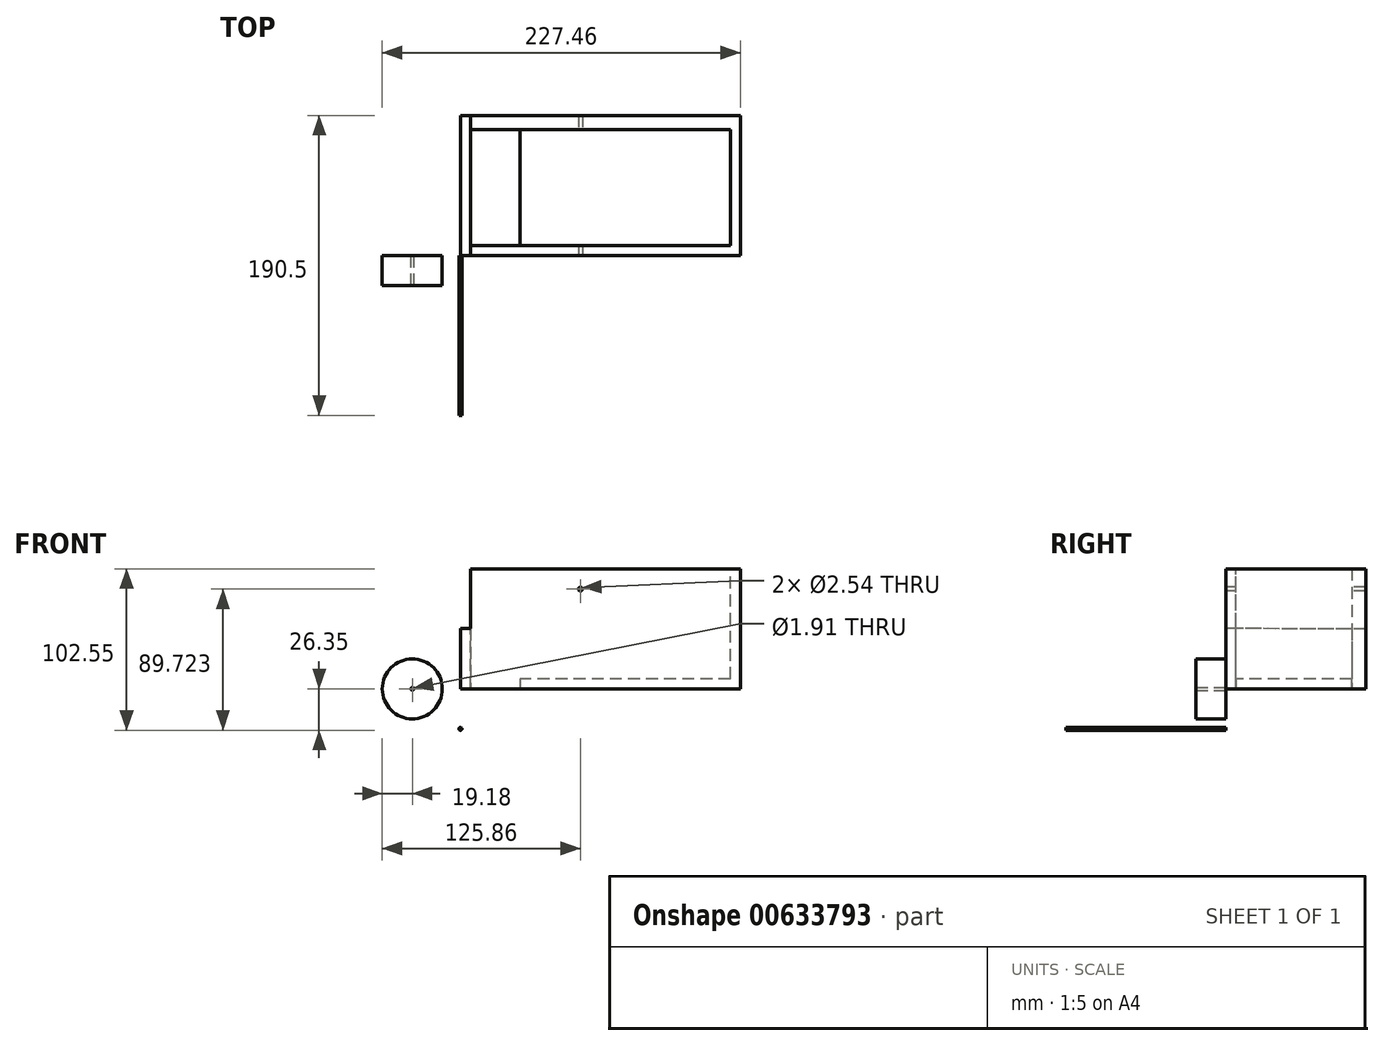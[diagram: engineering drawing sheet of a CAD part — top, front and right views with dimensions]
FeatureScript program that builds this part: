
annotation { "Feature Type Name" : "Feature", "Feature Type Description" : "" }
export const myFeature = defineFeature(function(context is Context, id is Id, definition is map)
    precondition{}
    {
        {
            var Q0;
            Q0=qCreatedBy(makeId("Front.planeOp"),FACE);
            var sketch = newSketch(context, id + "F0", { "sketchPlane" : qUnion([Q0])});
            skLineSegment(sketch, "E0", {"start": v(0, 0) * mm, "end": v(177.8, 0) * mm});
            skLineSegment(sketch, "E1", {"start": v(177.8, 0) * mm, "end": v(177.8, 76.2) * mm});
            skLineSegment(sketch, "E2", {"start": v(177.8, 76.2) * mm, "end": v(0, 76.2) * mm});
            skLineSegment(sketch, "E3", {"start": v(0, 76.2) * mm, "end": v(0, 0) * mm});
            skSolve(sketch);
        }
        {
            var Q0;
            Q0 = qSketchRegion(id + "F0", true);
            extrude(context, id + "F1", {"entities" : qUnion([Q0]), "oppositeDirection" : true, "depth" : 6.35 * mm, "offsetDistance" : 25.4 * mm});
        }
        {
            var Q0;
            Q0=qCreatedBy(makeId("Top.planeOp"),FACE);
            var sketch = newSketch(context, id + "F2", { "sketchPlane" : qUnion([Q0])});
            skLineSegment(sketch, "E4", {"start": v(0, 0) * mm, "end": v(0, 88.9) * mm});
            skLineSegment(sketch, "E5", {"start": v(0, 88.9) * mm, "end": v(177.8, 88.9) * mm});
            skLineSegment(sketch, "E6", {"start": v(177.8, 88.9) * mm, "end": v(177.8, 0) * mm});
            skLineSegment(sketch, "E7", {"start": v(0, 88.9) * mm, "end": v(6.35, 88.9) * mm});
            skLineSegment(sketch, "E8", {"start": v(6.35, 88.9) * mm, "end": v(6.35, 0) * mm});
            skLineSegment(sketch, "E9", {"start": v(0, 88.9) * mm, "end": v(0, 80.01) * mm});
            skLineSegment(sketch, "E10", {"start": v(0, 80.01) * mm, "end": v(171.45, 80.01) * mm});
            skLineSegment(sketch, "E11", {"start": v(171.45, 80.01) * mm, "end": v(171.45, 0) * mm});
            skLineSegment(sketch, "E12", {"start": v(0, 0) * mm, "end": v(6.35, 0) * mm});
            skLineSegment(sketch, "E13", {"start": v(171.45, 80.01) * mm, "end": v(177.8, 80.01) * mm});
            skLineSegment(sketch, "E14", {"start": v(177.8, 80.01) * mm, "end": v(171.45, 80.01) * mm});
            skLineSegment(sketch, "E15", {"start": v(171.45, 88.9) * mm, "end": v(171.45, 0) * mm});
            skLineSegment(sketch, "E16", {"start": v(177.8, 0) * mm, "end": v(171.45, 0) * mm});
            skSolve(sketch);
        }
        {
            var Q0;
            Q0 = qSketchRegion(id + "F2", true);
            extrude(context, id + "F3", {"entities" : qUnion([Q0]), "operationType" : NewBodyOperationType.ADD, "depth" : 76.2 * mm, "offsetDistance" : 25.4 * mm});
        }
        {
            var Q0;
            Q0=qCreatedBy(makeId("Top.planeOp"),FACE);
            var sketch = newSketch(context, id + "F4", { "sketchPlane" : qUnion([Q0])});
            skLineSegment(sketch, "E17", {"start": v(177.43, 0) * mm, "end": v(37.73, 0) * mm});
            skLineSegment(sketch, "E18", {"start": v(37.73, 0) * mm, "end": v(37.73, 88.76) * mm});
            skLineSegment(sketch, "E19", {"start": v(37.73, 88.76) * mm, "end": v(177.51, 88.76) * mm});
            skLineSegment(sketch, "E20", {"start": v(177.51, 88.76) * mm, "end": v(177.43, 0) * mm});
            skSolve(sketch);
        }
        {
            var Q0;
            Q0 = qSketchRegion(id + "F4", true);
            extrude(context, id + "F5", {"entities" : qUnion([Q0]), "operationType" : NewBodyOperationType.ADD, "depth" : 6.35 * mm, "offsetDistance" : 25.4 * mm});
        }
        {
            var Q0;
            Q0=qCreatedBy(makeId("Right.planeOp"),FACE);
            var sketch = newSketch(context, id + "F6", { "sketchPlane" : qUnion([Q0])});
            skLineSegment(sketch, "E21", {"start": v(0, 0) * mm, "end": v(0, 38.1) * mm});
            skLineSegment(sketch, "E22", {"start": v(0, 38.1) * mm, "end": v(0, 76.2) * mm});
            skLineSegment(sketch, "E23", {"start": v(0, 76.2) * mm, "end": v(88.9, 76.2) * mm});
            skLineSegment(sketch, "E24", {"start": v(88.9, 76.2) * mm, "end": v(88.9, 38.1) * mm});
            skLineSegment(sketch, "E25", {"start": v(88.9, 38.1) * mm, "end": v(0, 38.1) * mm});
            skSolve(sketch);
        }
        {
            var Q0;
            Q0=makeQuery(id+"F6.imprint","IMPRINT",FACE,{"disambiguationData":[TD([[makeQuery(id+"F6.imprint","IMPRINT",EDGE,{"derivedFrom":sQuery(id+"F6.wireOp",EDGE,"E22")}),-1.0]])]});
            extrude(context, id + "F7", {"entities" : qUnion([Q0]), "operationType" : NewBodyOperationType.REMOVE, "oppositeDirection" : true, "depth" : 6.35 * mm, "offsetDistance" : 25.4 * mm});
        }
        {
            var Q0;
            Q0=qCreatedBy(makeId("Front.planeOp"),FACE);
            var sketch = newSketch(context, id + "F8", { "sketchPlane" : qUnion([Q0])});
            skLineSegment(sketch, "E26", {"start": v(0, 76.07) * mm, "end": v(76.2, 76.07) * mm});
            skLineSegment(sketch, "E27", {"start": v(76.2, 76.07) * mm, "end": v(76.2, 63.37) * mm});
            skCircle(sketch, "E28", {"center": v(76.2, 63.37) * mm, "radius": 1.27 * mm});
            skSolve(sketch);
        }
        {
            var Q0;
            Q0=qCreatedBy(makeId("Front.planeOp"),FACE);
            var sketch = newSketch(context, id + "F9", { "sketchPlane" : qUnion([Q0])});
            skLineSegment(sketch, "E29", {"start": v(-5.2, 0) * mm, "end": v(-30.6, 0) * mm});
            skCircle(sketch, "E30", {"center": v(-30.6, 0) * mm, "radius": 19.05 * mm});
            skLineSegment(sketch, "E31", {"start": v(0, 76.7) * mm, "end": v(76.2, 76.7) * mm});
            skLineSegment(sketch, "E32", {"start": v(76.2, 76.7) * mm, "end": v(76.2, 70.35) * mm});
            skCircle(sketch, "E33", {"center": v(76.2, 70.35) * mm, "radius": 1.27 * mm});
            skSolve(sketch);
        }
        {
            var Q0;
            Q0=makeQuery(id+"F9.imprint","IMPRINT",FACE,{"disambiguationData":[TD([[makeQuery(id+"F9.imprint","IMPRINT",EDGE,{"derivedFrom":sQuery(id+"F9.wireOp",EDGE,"E30")}),1.0]])]});
            extrude(context, id + "F10", {"entities" : qUnion([Q0]), "depth" : 19.05 * mm, "offsetDistance" : 25.4 * mm});
        }
        {
            var Q0;
            Q0=makeQuery(id+"F8.imprint","IMPRINT",FACE,{"disambiguationData":[TD([[makeQuery(id+"F8.imprint","IMPRINT",EDGE,{"derivedFrom":sQuery(id+"F8.wireOp",EDGE,"E28")}),1.0]])]});
            extrude(context, id + "F11", {"entities" : qUnion([Q0]), "operationType" : NewBodyOperationType.REMOVE, "oppositeDirection" : true, "depth" : 254 * mm, "offsetDistance" : 25.4 * mm});
        }
        {
            var Q0;
            Q0=qCreatedBy(makeId("Right.planeOp"),FACE);
            var sketch = newSketch(context, id + "F12", { "sketchPlane" : qUnion([Q0])});
            skLineSegment(sketch, "E34", {"start": v(88.84, 0) * mm, "end": v(0, 0) * mm});
            skLineSegment(sketch, "E35", {"start": v(0, 0) * mm, "end": v(0, 76.2) * mm});
            skLineSegment(sketch, "E36", {"start": v(0, 76.2) * mm, "end": v(88.96, 76.2) * mm});
            skLineSegment(sketch, "E37", {"start": v(88.96, 76.2) * mm, "end": v(88.84, 0) * mm});
            skLineSegment(sketch, "E38", {"start": v(88.9, 38.1) * mm, "end": v(0, 38.25) * mm});
            skLineSegment(sketch, "E39", {"start": v(0, 38.25) * mm, "end": v(0, 76.2) * mm});
            skSolve(sketch);
        }
        {
            var Q0;
            {var subQ0=sQuery(id+"F12.wireOp",EDGE,"E36");Q0=makeQuery(id+"F12.imprint","IMPRINT",FACE,{"disambiguationData":[TD([[makeQuery(id+"F12.imprint","IMPRINT",EDGE,{"derivedFrom":subQ0}),-1.0]])]});}
            var sketch = newSketch(context, id + "F13", { "sketchPlane" : qUnion([Q0])});
            skSolve(sketch);
        }
        {
            var Q0;
            {var subQ0=sQuery(id+"F12.wireOp",EDGE,"E36");Q0=makeQuery(id+"F12.imprint","IMPRINT",FACE,{"disambiguationData":[TD([[makeQuery(id+"F12.imprint","IMPRINT",EDGE,{"derivedFrom":subQ0}),-1.0]])]});}
            extrude(context, id + "F14", {"entities" : qUnion([Q0]), "operationType" : NewBodyOperationType.REMOVE, "oppositeDirection" : true, "depth" : 6.35 * mm, "offsetDistance" : 25.4 * mm});
        }
        {
            var Q0;
            {var subQ0=sQuery(id+"F12.wireOp",EDGE,"E36");Q0=makeQuery(id+"F13.imprint","IMPRINT",FACE,{"disambiguationData":[TD([[makeQuery(id+"F13.imprint","IMPRINT",EDGE,{"derivedFrom":makeQuery(id+"F12.imprint","IMPRINT",EDGE,{"derivedFrom":subQ0})}),-1.0]])]});}
            extrude(context, id + "F15", {"entities" : qUnion([Q0]), "operationType" : NewBodyOperationType.REMOVE, "depth" : 6.35 * mm, "offsetDistance" : 25.4 * mm});
        }
        {
            var Q0;
            Q0=qCreatedBy(makeId("Front.planeOp"),FACE);
            var sketch = newSketch(context, id + "F16", { "sketchPlane" : qUnion([Q0])});
            skCircle(sketch, "E40", {"center": v(-30.68, 0) * mm, "radius": 1.27 * mm});
            skSolve(sketch);
        }
        {
            var Q0;
            Q0 = qSketchRegion(id + "F16", true);
            extrude(context, id + "F17", {"entities" : qUnion([Q0]), "operationType" : NewBodyOperationType.REMOVE, "oppositeDirection" : true, "depth" : 76.2 * mm, "offsetDistance" : 25.4 * mm});
        }
        {
            var Q0;
            Q0 = qSketchRegion(id + "F16", true);
            extrude(context, id + "F18", {"entities" : qUnion([Q0]), "operationType" : NewBodyOperationType.REMOVE, "oppositeDirection" : true, "depth" : 76.2 * mm, "offsetDistance" : 25.4 * mm});
        }
        {
            var Q0;
            Q0=qCreatedBy(makeId("Front.planeOp"),FACE);
            var sketch = newSketch(context, id + "F19", { "sketchPlane" : qUnion([Q0])});
            skLineSegment(sketch, "E41", {"start": v(0, 0) * mm, "end": v(0, -25.4) * mm});
            skCircle(sketch, "E42", {"center": v(0, -25.4) * mm, "radius": 0.95 * mm});
            skLineSegment(sketch, "E43", {"start": v(0, 0) * mm, "end": v(-30.48, 0) * mm});
            skCircle(sketch, "E44", {"center": v(-30.48, 0) * mm, "radius": 0.95 * mm});
            skSolve(sketch);
        }
        {
            var Q0;
            Q0=makeQuery(id+"F19.imprint","IMPRINT",FACE,{"disambiguationData":[TD([[makeQuery(id+"F19.imprint","IMPRINT",EDGE,{"derivedFrom":sQuery(id+"F19.wireOp",EDGE,"E42")}),1.0]])]});
            extrude(context, id + "F20", {"entities" : qUnion([Q0]), "depth" : 101.6 * mm, "offsetDistance" : 25.4 * mm});
        }
        {
            var Q0;
            Q0=qCreatedBy(makeId("Front.planeOp"),FACE);
            var sketch = newSketch(context, id + "F21", { "sketchPlane" : qUnion([Q0])});
            skLineSegment(sketch, "E45", {"start": v(0, 0) * mm, "end": v(-30.48, 0) * mm});
            skCircle(sketch, "E46", {"center": v(-30.48, 0) * mm, "radius": 0.95 * mm});
            skSolve(sketch);
        }
        {
            var Q0;
            Q0 = qSketchRegion(id + "F21", true);
            extrude(context, id + "F22", {"entities" : qUnion([Q0]), "operationType" : NewBodyOperationType.REMOVE, "oppositeDirection" : true, "depth" : 76.2 * mm, "offsetDistance" : 25.4 * mm});
        }
        {
            var Q0;
            Q0 = qSketchRegion(id + "F21", true);
            extrude(context, id + "F23", {"entities" : qUnion([Q0]), "operationType" : NewBodyOperationType.REMOVE, "depth" : 101.6 * mm, "offsetDistance" : 25.4 * mm});
        }
    });
